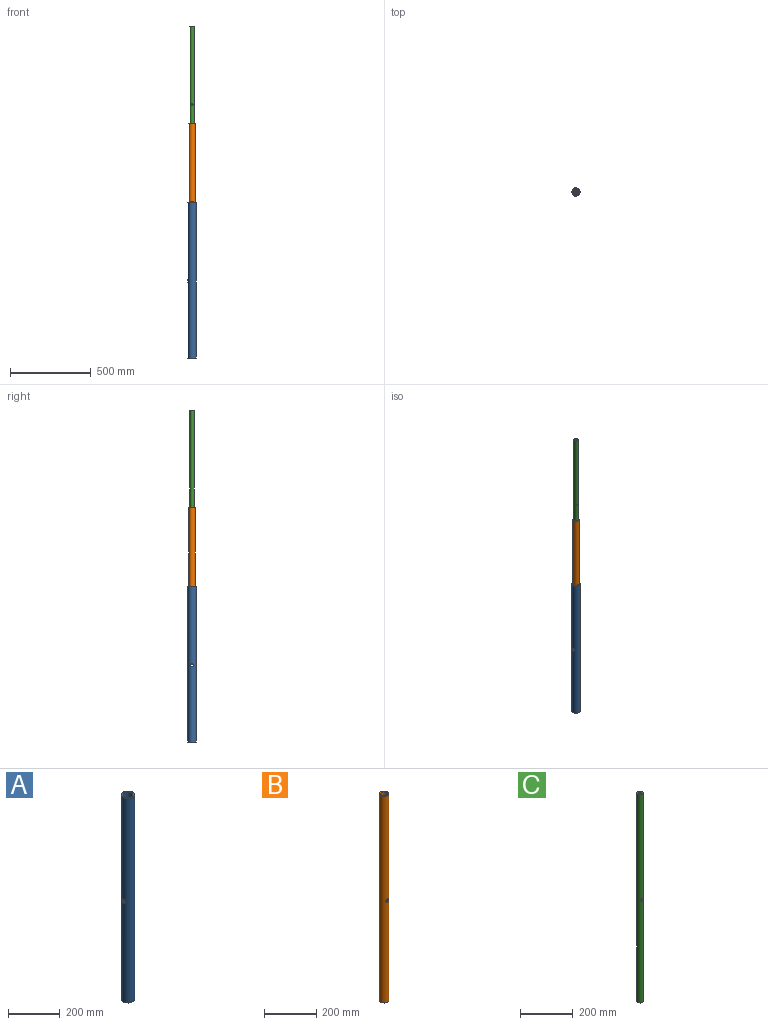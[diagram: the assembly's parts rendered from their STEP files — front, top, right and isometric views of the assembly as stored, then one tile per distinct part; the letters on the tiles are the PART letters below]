
ASSEMBLY  parts=3 mates=2
PART A: 6 faces, bbox 50.8x50.8x965.2 mm
  f0: cylinder r=19.05mm len=965.2mm, axis (0,0,-1), area 115056.4mm2, adj f2,f3,f4,f5
  f1: cylinder r=25.4mm len=965.2mm, axis (0,0,-1), area 153572.2mm2, adj f2,f3,f4,f5
  f2: plane 50.8x50.8mm, normal (0,0,1), area 886.7mm2, adj f0,f1
  f3: plane 50.8x50.8mm, normal (0,0,-1), area 886.7mm2, adj f0,f1
  f4: cylinder r=8.56mm len=17.12mm, axis (1,0,0), area 355.7mm2, adj f0,f1
  f5: cylinder r=8.56mm len=17.12mm, axis (1,0,0), area 355.7mm2, adj f0,f1
PART B: 6 faces, bbox 38.1x38.1x965.2 mm
  f0: cylinder r=12.7mm len=965.2mm, axis (0,0,-1), area 76670.8mm2, adj f2,f3,f4,f5
  f1: cylinder r=19.05mm len=965.2mm, axis (0,0,-1), area 115189.6mm2, adj f2,f3,f4,f5
  f2: plane 38.1x38.1mm, normal (0,0,1), area 633.4mm2, adj f0,f1
  f3: plane 38.1x38.1mm, normal (0,0,-1), area 633.4mm2, adj f0,f1
  f4: cylinder r=7.29mm len=14.58mm, axis (0,1,0), area 309.4mm2, adj f0,f1
  f5: cylinder r=7.29mm len=14.58mm, axis (0,1,0), area 309.2mm2, adj f0,f1
PART C: 7 faces, bbox 25.4x25.4x965.2 mm
  f0: cylinder r=6.35mm len=488.95mm, axis (0,0,-1), area 19346.9mm2, adj f3,f5,f6
  f1: cylinder r=6.35mm len=476.25mm, axis (0,0,-1), area 18840.2mm2, adj f4,f5,f6
  f2: cylinder r=12.7mm len=965.2mm, axis (0,0,-1), area 76757.2mm2, adj f3,f4,f5,f6
  f3: plane 25.4x25.4mm, normal (0,0,1), area 380mm2, adj f0,f2
  f4: plane 25.4x25.4mm, normal (0,0,-1), area 380mm2, adj f1,f2
  f5: cylinder r=6.35mm len=12.7mm, axis (0,-1,0), area 312.1mm2, adj f0,f1,f2
  f6: cylinder r=6.35mm len=12.7mm, axis (0,-1,0), area 312.1mm2, adj f0,f1,f2
PLACE A t=(-502.88,40.17,-952.04)mm fixed
PLACE B t=(-502.88,40.17,-463.09)mm
PLACE C t=(-502.88,40.17,142.7)mm
MATE slider A.f1 <-> B.f1  axis (0,0,1) through (-502.88,40.17,13.16)mm
MATE slider C.f2 <-> B.f0  axis (0,0,-1) through (-502.88,40.17,142.7)mm
